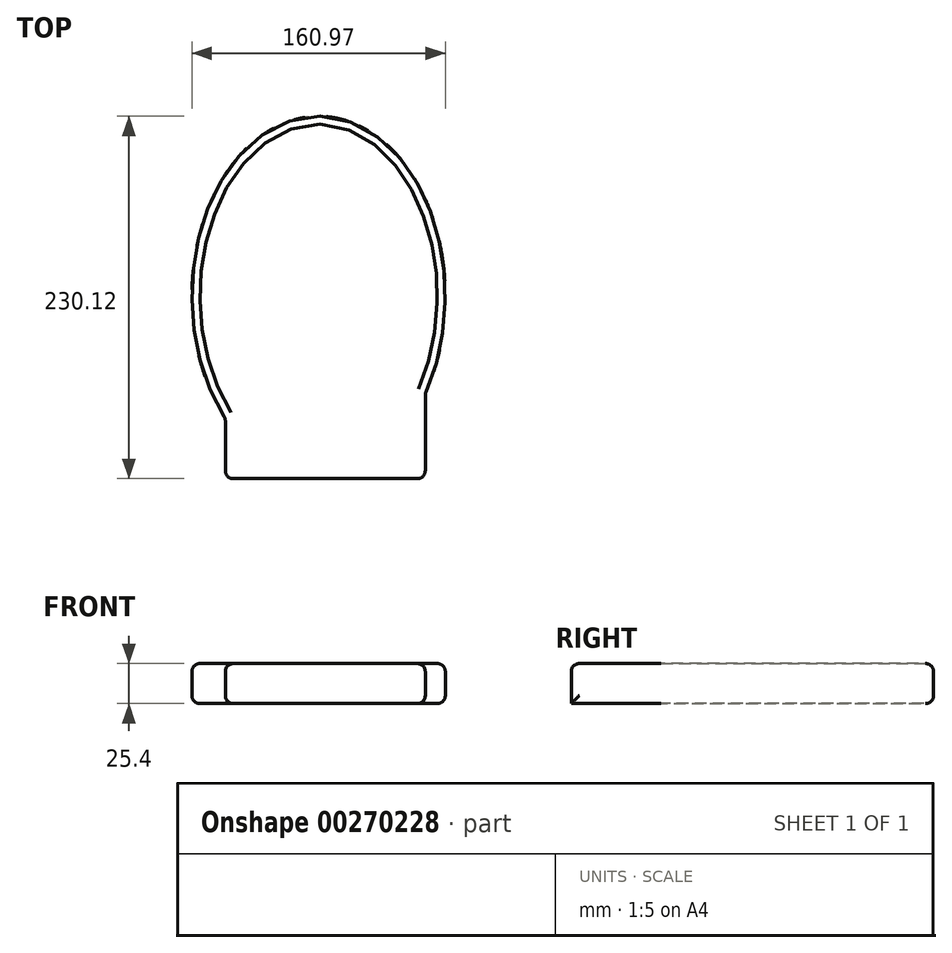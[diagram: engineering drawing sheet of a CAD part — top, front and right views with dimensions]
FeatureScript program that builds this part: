
annotation { "Feature Type Name" : "Feature", "Feature Type Description" : "" }
export const myFeature = defineFeature(function(context is Context, id is Id, definition is map)
    precondition{}
    {
        {
            var Q0;
            Q0=qCreatedBy(makeId("Top.planeOp"),FACE);
            var sketch = newSketch(context, id + "F0", { "sketchPlane" : qUnion([Q0])});
            skLineSegment(sketch, "E0", {"start": v(0, 0) * mm, "end": v(76.2, 0) * mm});
            skLineSegment(sketch, "E1", {"start": v(0, 0) * mm, "end": v(0, 114.3) * mm});
            skEllipse(sketch, "E2", {"center": v(-4.28, 0) * mm, "majorRadius": 80.48 * mm, "minorRadius": 114.46 * mm, "majorAxis": v(1, 0)});
            skLineSegment(sketch, "E3.bottom", {"start": v(63.5, -115.66) * mm, "end": v(-63.5, -115.66) * mm});
            skLineSegment(sketch, "E3.top", {"start": v(63.5, -36.65) * mm, "end": v(-63.5, -36.65) * mm});
            skLineSegment(sketch, "E3.left", {"start": v(63.5, -115.66) * mm, "end": v(63.5, -36.65) * mm});
            skLineSegment(sketch, "E3.right", {"start": v(-63.5, -115.66) * mm, "end": v(-63.5, -36.65) * mm});
            skPoint(sketch, "E3.middle", {"position": v(0, -76.16) * mm});
            skSolve(sketch);
        }
        {
            var Q0;
            {var subQ0=sQuery(id+"F0.wireOp",EDGE,"E0");Q0=makeQuery(id+"F0.imprint","IMPRINT",FACE,{"disambiguationData":[TD([[makeQuery(id+"F0.imprint","IMPRINT",EDGE,{"derivedFrom":subQ0}),-1.0]])]});}
            var Q1;
            {var subQ0=sQuery(id+"F0.wireOp",EDGE,"E0");Q1=makeQuery(id+"F0.imprint","IMPRINT",FACE,{"disambiguationData":[TD([[makeQuery(id+"F0.imprint","IMPRINT",EDGE,{"derivedFrom":subQ0}),1.0]])]});}
            var Q2;
            {var subQ5=sQuery(id+"F0.wireOp",EDGE,"E3.bottom");Q2=makeQuery(id+"F0.imprint","IMPRINT",FACE,{"disambiguationData":[TD([[makeQuery(id+"F0.imprint","IMPRINT",EDGE,{"derivedFrom":subQ5}),-1.0]])]});}
            var Q3;
            {var subQ5=sQuery(id+"F0.wireOp",EDGE,"E3.top");Q3=makeQuery(id+"F0.imprint","IMPRINT",FACE,{"disambiguationData":[TD([[makeQuery(id+"F0.imprint","IMPRINT",EDGE,{"derivedFrom":subQ5}),1.0]])]});}
            extrude(context, id + "F1", {"entities" : qUnion([Q0, Q1, Q2, Q3]), "depth" : 25.4 * mm});
        }
        {
            var Q0;
            Q0=makeQuery(id+"F1.opExtrude","SWEPT_EDGE",EDGE,{"disambiguationData":[OSD([sQuery(id+"F0.wireOp",EDGE,"E3.bottom"),sQuery(id+"F0.wireOp",EDGE,"E3.left")])]});
            var Q1;
            Q1=makeQuery(id+"F1.opExtrude","SWEPT_EDGE",EDGE,{"disambiguationData":[OSD([sQuery(id+"F0.wireOp",EDGE,"E3.bottom"),sQuery(id+"F0.wireOp",EDGE,"E3.right")])]});
            var Q2;
            Q2=makeQuery(id+"F1.opExtrude","CAP_EDGE",EDGE,{"disambiguationData":[OSD([sQuery(id+"F0.wireOp",EDGE,"E2")])],"isStart":true});
            var Q3;
            Q3=makeQuery(id+"F1.opExtrude","CAP_EDGE",EDGE,{"disambiguationData":[OSD([sQuery(id+"F0.wireOp",EDGE,"E2")])],"isStart":false});
            var Q4;
            Q4=makeQuery(id+"F1.opExtrude","CAP_EDGE",EDGE,{"disambiguationData":[OSD([sQuery(id+"F0.wireOp",EDGE,"E3.bottom")])],"isStart":false});
            var Q5;
            Q5=makeQuery(id+"F1.opExtrude","CAP_EDGE",EDGE,{"disambiguationData":[OSD([sQuery(id+"F0.wireOp",EDGE,"E3.right")])],"isStart":true});
            var Q6;
            Q6=makeQuery(id+"F1.opExtrude","CAP_EDGE",EDGE,{"disambiguationData":[OSD([sQuery(id+"F0.wireOp",EDGE,"E3.right")])],"isStart":false});
            var Q7;
            Q7=makeQuery(id+"F1.opExtrude","SWEPT_EDGE",EDGE,{"disambiguationData":[OSD([sQuery(id+"F0.wireOp",EDGE,"E2"),sQuery(id+"F0.wireOp",EDGE,"E3.left")])]});
            var Q8;
            Q8=makeQuery(id+"F1.opExtrude","SWEPT_EDGE",EDGE,{"disambiguationData":[OSD([sQuery(id+"F0.wireOp",EDGE,"E2"),sQuery(id+"F0.wireOp",EDGE,"E3.right")])]});
            var Q9;
            Q9=makeQuery(id+"F1.opExtrude","CAP_EDGE",EDGE,{"disambiguationData":[OSD([sQuery(id+"F0.wireOp",EDGE,"E3.left")])],"isStart":true});
            var Q10;
            Q10=makeQuery(id+"F1.opExtrude","CAP_EDGE",EDGE,{"disambiguationData":[OSD([sQuery(id+"F0.wireOp",EDGE,"E3.left")])],"isStart":false});
            fillet(context, id + "F2", {"entities" : qUnion([Q0, Q1, Q2, Q3, Q4, Q5, Q6, Q7, Q8, Q9, Q10]), "radius" : 5.08 * mm, "tangentPropagation" : true, "allowEdgeOverflow" : false});
        }
    });
